# Revit family: EB-705_Ciclon LS
name_source: partatom
category: Plumbing Fixtures
revit_build: Autodesk Revit 2015 (Build: 20140606_1530(x64)
units: mm (PartAtom-declared; Revit-internal decimal feet)

## types (1)
- EB-705 CICLON LS
    Apparent power = 200 VA
    Certificates = http://www.jimten.com
    Dameter Side inlet T = 40 mm  [stored 0.131234 ft]
    Depht = 180 mm
    Description = LIFTING STATION FOR SANITARY APPLIANCE
    Diameter Impulsion = 32 mm  [stored 0.104987 ft]
    Diameter Side inlet R = 40 mm  [stored 0.131234 ft]
    Flowrate = 2.5 L/s
    Height = 278 mm
    Inlets = 5 x Ø40 mm
    Load classification = Electrical appliances
    Manufacturer = Jimten
    Material = PP (White)
    MaxPumping Height = 7 m vertical
    Model = EB-705 CICLON LS
    Network = 220-240 VAC 50HZ
    Number of poles = 1
    Outlet = 1 x Ø32mm
    Power = 390 W
    Reference = 75401
    Sanitary Appliance = Yes
    Type Comments = EASY MAINTENANCE THANKS TO ITS CASET SYSTEM. SILENT.
    U.Outlet Bidet-Shower = 2
    U.Outlet Wash basin = 1
    URL = http://www.jimten.com
    Voltage = 230 V
    WC = No

note: [stored X ft] marks values corroborated as IEEE doubles in the binary element streams (Revit-internal decimal feet)

## geometry (parser evidence)
native form markers: Blend x3, Sweep x2
no freeform markers — native parametric forms only
